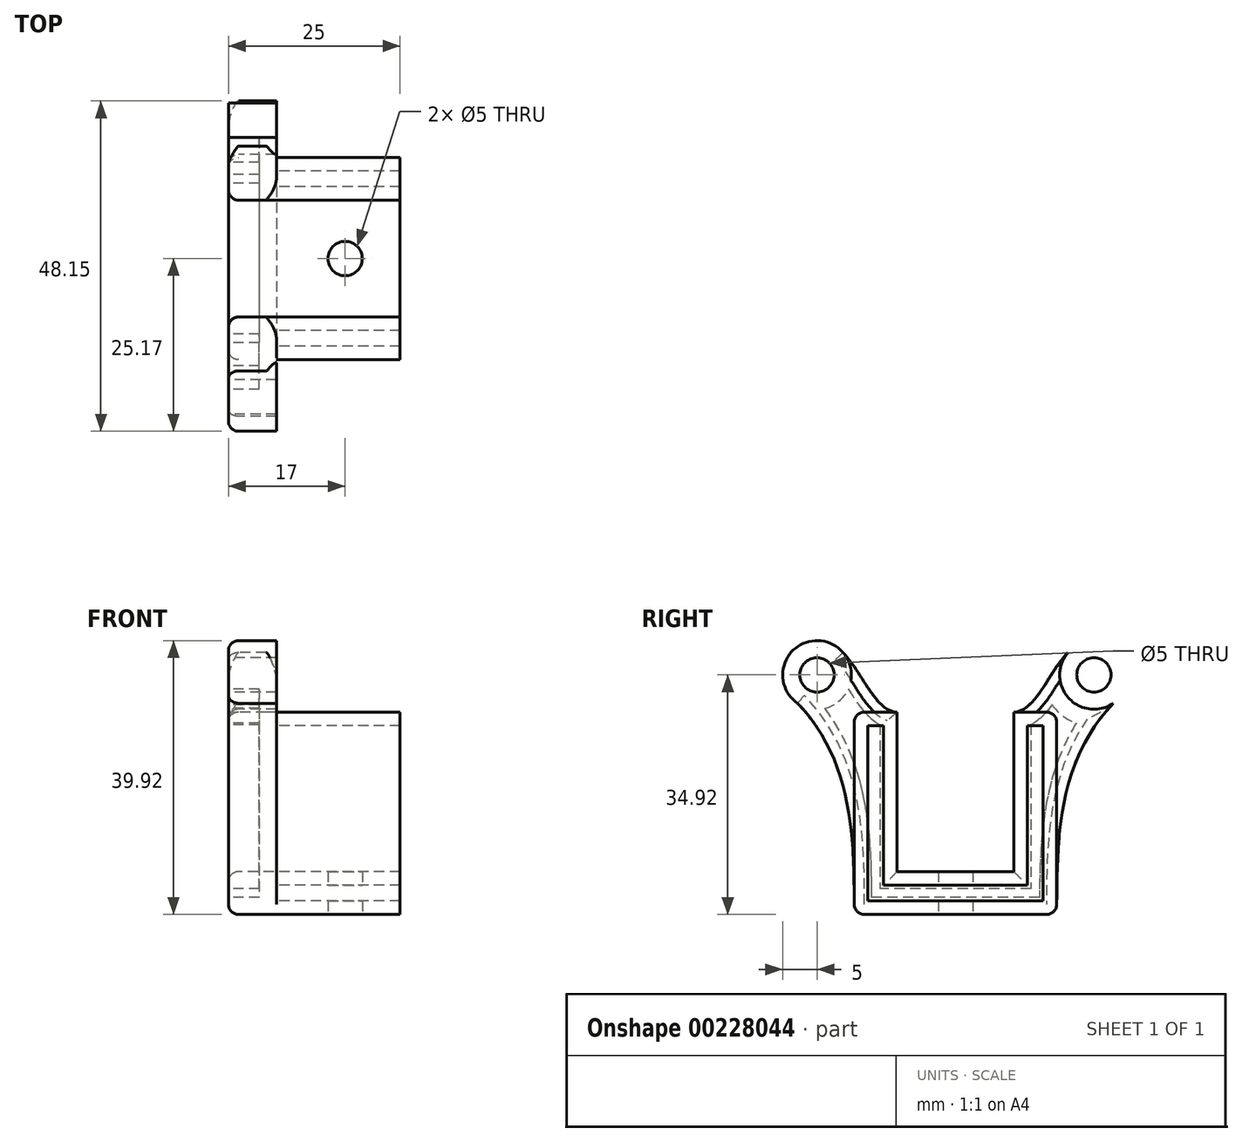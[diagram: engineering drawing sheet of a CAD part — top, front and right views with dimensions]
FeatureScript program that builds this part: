
annotation { "Feature Type Name" : "Feature", "Feature Type Description" : "" }
export const myFeature = defineFeature(function(context is Context, id is Id, definition is map)
    precondition{}
    {
        {
            var Q0;
            Q0=qCreatedBy(makeId("Right.planeOp"),FACE);
            var sketch = newSketch(context, id + "F0", { "sketchPlane" : qUnion([Q0])});
            skLineSegment(sketch, "E0.top", {"start": v(12.75, -12.75) * mm, "end": v(-12.75, -12.75) * mm});
            skLineSegment(sketch, "E0.left", {"start": v(12.75, 12.75) * mm, "end": v(12.75, -12.75) * mm});
            skLineSegment(sketch, "E0.right", {"start": v(-12.75, 12.75) * mm, "end": v(-12.75, -12.75) * mm});
            skPoint(sketch, "E0.middle", {"position": v(0, 0) * mm});
            skLineSegment(sketch, "E1.0", {"start": v(10.5, 12.75) * mm, "end": v(10.5, -10.5) * mm});
            skLineSegment(sketch, "E1.1", {"start": v(10.5, -10.5) * mm, "end": v(-10.5, -10.5) * mm});
            skLineSegment(sketch, "E1.2", {"start": v(-10.5, 12.75) * mm, "end": v(-10.5, -10.5) * mm});
            skLineSegment(sketch, "E2", {"start": v(-12.75, 12.75) * mm, "end": v(-10.5, 12.75) * mm});
            skLineSegment(sketch, "E3", {"start": v(10.5, 12.75) * mm, "end": v(12.75, 12.75) * mm});
            skLineSegment(sketch, "E4.0", {"start": v(-14.75, 14.75) * mm, "end": v(-8.5, 14.75) * mm});
            skLineSegment(sketch, "E4.1", {"start": v(-14.75, 14.75) * mm, "end": v(-14.75, -14.75) * mm});
            skLineSegment(sketch, "E4.2", {"start": v(-8.5, 14.75) * mm, "end": v(-8.5, -8.5) * mm});
            skLineSegment(sketch, "E4.3", {"start": v(14.75, -14.75) * mm, "end": v(-14.75, -14.75) * mm});
            skLineSegment(sketch, "E4.4", {"start": v(8.5, -8.5) * mm, "end": v(-8.5, -8.5) * mm});
            skLineSegment(sketch, "E4.5", {"start": v(8.5, 14.75) * mm, "end": v(8.5, -8.5) * mm});
            skLineSegment(sketch, "E4.6", {"start": v(8.5, 14.75) * mm, "end": v(14.75, 14.75) * mm});
            skLineSegment(sketch, "E4.7", {"start": v(14.75, 14.75) * mm, "end": v(14.75, -14.75) * mm});
            skLineSegment(sketch, "E5", {"start": v(-8.5, 14.75) * mm, "end": v(8.5, 14.75) * mm});
            skLineSegment(sketch, "E6", {"start": v(14.75, -14.75) * mm, "end": v(-49.35, 49.35) * mm, "construction": true});
            skLineSegment(sketch, "E7", {"start": v(-14.75, -14.75) * mm, "end": v(48.22, 48.22) * mm, "construction": true});
            skLineSegment(sketch, "E8", {"start": v(-40.93, 20.17) * mm, "end": v(49.97, 20.17) * mm, "construction": true});
            skCircle(sketch, "E9", {"center": v(-20.17, 20.17) * mm, "radius": 5 * mm});
            skLineSegment(sketch, "E10", {"start": v(0, 73.34) * mm, "end": v(0, -65.97) * mm, "construction": true});
            skPoint(sketch, "E11.0.internal.snap0", {"position": v(-17.3, 17.3) * mm});
            skFitSpline(sketch, "E11", {"points": [v(-24.26, 17.3) * mm, v(-14.75, -14.75) * mm], "startDerivative": vector(28.54, -26.5) * mm, "endDerivative": vector(0, -33.68) * mm});
            skFitSpline(sketch, "E12", {"points": [v(-16.39, 23.44) * mm, v(-8.5, 14.75) * mm], "startDerivative": vector(8.29, -8.38) * mm, "endDerivative": vector(9.37, 0) * mm});
            skCircle(sketch, "E13", {"center": v(-20.17, 20.17) * mm, "radius": 2.5 * mm});
            skFitSpline(sketch, "E14.MirrorCS", {"points": [v(16.39, 23.44) * mm, v(8.5, 14.75) * mm], "startDerivative": vector(-8.29, -8.38) * mm, "endDerivative": vector(-9.37, 0) * mm});
            skFitSpline(sketch, "E15.MirrorCS", {"points": [v(24.26, 17.3) * mm, v(14.75, -14.75) * mm], "startDerivative": vector(-28.54, -26.5) * mm, "endDerivative": vector(0, -33.68) * mm});
            skCircle(sketch, "E16.MirrorC", {"center": v(20.17, 20.17) * mm, "radius": 2.5 * mm});
            skCircle(sketch, "E17.MirrorC", {"center": v(20.17, 20.17) * mm, "radius": 5 * mm});
            skSolve(sketch);
        }
        {
            var Q0;
            Q0=makeQuery(id+"F0.imprint","IMPRINT",FACE,{"disambiguationData":[TD([[makeQuery(id+"F0.imprint","IMPRINT",EDGE,{"derivedFrom":sQuery(id+"F0.wireOp",EDGE,"E0.top")}),1.0]])]});
            extrude(context, id + "F1", {"entities" : qUnion([Q0]), "depth" : 25 * mm});
        }
        {
            var Q0;
            Q0=makeQuery(id+"F0.imprint","IMPRINT",FACE,{"disambiguationData":[TD([[makeQuery(id+"F0.imprint","IMPRINT",EDGE,{"derivedFrom":sQuery(id+"F0.wireOp",EDGE,"E4.0")}),1.0]])]});
            var Q1;
            Q1=makeQuery(id+"F0.imprint","IMPRINT",FACE,{"disambiguationData":[TD([[makeQuery(id+"F0.imprint","IMPRINT",EDGE,{"derivedFrom":sQuery(id+"F0.wireOp",EDGE,"E13")}),-1.0]])]});
            var Q2;
            {var subQ5=sQuery(id+"F0.wireOp",EDGE,"E4.7");Q2=makeQuery(id+"F0.imprint","IMPRINT",FACE,{"disambiguationData":[TD([[makeQuery(id+"F0.imprint","IMPRINT",EDGE,{"derivedFrom":subQ5}),1.0]])]});}
            var Q3;
            Q3=makeQuery(id+"F0.imprint","IMPRINT",FACE,{"disambiguationData":[TD([[makeQuery(id+"F0.imprint","IMPRINT",EDGE,{"derivedFrom":sQuery(id+"F0.wireOp",EDGE,"E16.MirrorC")}),1.0]])]});
            var Q4;
            Q4=makeQuery(id+"F0.imprint","IMPRINT",FACE,{"disambiguationData":[TD([[makeQuery(id+"F0.imprint","IMPRINT",EDGE,{"derivedFrom":sQuery(id+"F0.wireOp",EDGE,"E0.top")}),-1.0]])]});
            extrude(context, id + "F2", {"entities" : qUnion([Q0, Q1, Q2, Q3, Q4]), "operationType" : NewBodyOperationType.ADD, "depth" : 7 * mm});
        }
        {
            var Q0;
            {var subQ0=sQuery(id+"F0.wireOp",EDGE,"E14.MirrorCS");var subQ1=sQuery(id+"F0.wireOp",EDGE,"E4.7");var subQ2=sQuery(id+"F0.wireOp",EDGE,"E4.6");var subQ3=sQuery(id+"F0.wireOp",EDGE,"E4.1");var subQ4=sQuery(id+"F0.wireOp",EDGE,"E4.0");var subQ5=sQuery(id+"F0.wireOp",EDGE,"E3");var subQ6=sQuery(id+"F0.wireOp",EDGE,"E2");var subQ7=sQuery(id+"F0.wireOp",EDGE,"E1.2");var subQ8=sQuery(id+"F0.wireOp",EDGE,"E1.1");var subQ9=sQuery(id+"F0.wireOp",EDGE,"E1.0");var subQ10=sQuery(id+"F0.wireOp",EDGE,"E0.right");var subQ11=sQuery(id+"F0.wireOp",EDGE,"E0.left");var subQ12=sQuery(id+"F0.wireOp",EDGE,"E0.top");Q0=makeQuery(id+"F2.boolean.opBoolean","MERGE",FACE,{"derivedFrom":[makeQuery(id+"F1.opExtrude","CAP_FACE",FACE,{"disambiguationData":[OSD([subQ12,subQ11,subQ10,subQ9,subQ8,subQ7,subQ6,subQ5,subQ4,subQ3,sQuery(id+"F0.wireOp",EDGE,"E4.2"),sQuery(id+"F0.wireOp",EDGE,"E4.3"),sQuery(id+"F0.wireOp",EDGE,"E4.4"),sQuery(id+"F0.wireOp",EDGE,"E4.5"),subQ2,subQ1,subQ0])],"isStart":true}),makeQuery(id+"F2.opExtrude","CAP_FACE",FACE,{"disambiguationData":[OSD([subQ12,subQ11,subQ10,subQ9,subQ8,subQ7,subQ6,subQ5])],"isStart":true}),makeQuery(id+"F2.opExtrude","CAP_FACE",FACE,{"disambiguationData":[OSD([subQ4,subQ3,sQuery(id+"F0.wireOp",EDGE,"E9"),sQuery(id+"F0.wireOp",EDGE,"E11"),sQuery(id+"F0.wireOp",EDGE,"E12"),sQuery(id+"F0.wireOp",EDGE,"E13")])],"isStart":true}),makeQuery(id+"F2.opExtrude","CAP_FACE",FACE,{"disambiguationData":[OSD([subQ2,subQ1,subQ0,sQuery(id+"F0.wireOp",EDGE,"E15.MirrorCS"),sQuery(id+"F0.wireOp",EDGE,"E16.MirrorC"),sQuery(id+"F0.wireOp",EDGE,"E17.MirrorC")])],"isStart":true})]});}
            shell(context, id + "F3", {"entities" : qUnion([Q0]), "thickness" : 2.5 * mm});
        }
        {
            var Q0;
            Q0=makeQuery(id+"F1.opExtrude","SWEPT_FACE",FACE,{"disambiguationData":[OSD([sQuery(id+"F0.wireOp",EDGE,"E4.3")])]});
            var sketch = newSketch(context, id + "F4", { "sketchPlane" : qUnion([Q0])});
            skCircle(sketch, "E18", {"center": v(17, 0) * mm, "radius": 1.5 * mm});
            skSolve(sketch);
        }
        {
            var Q0;
            Q0=sQuery(id+"F4.wireOp",VERTEX,"E18.center");
            var Q1;
            Q1=makeQuery(id+"F1.opExtrude","SWEPT_BODY",BODY,{"disambiguationData":[OSD([sQuery(id+"F0.wireOp",EDGE,"E0.top"),sQuery(id+"F0.wireOp",EDGE,"E0.left"),sQuery(id+"F0.wireOp",EDGE,"E0.right"),sQuery(id+"F0.wireOp",EDGE,"E1.0"),sQuery(id+"F0.wireOp",EDGE,"E1.1"),sQuery(id+"F0.wireOp",EDGE,"E1.2"),sQuery(id+"F0.wireOp",EDGE,"E2"),sQuery(id+"F0.wireOp",EDGE,"E3"),sQuery(id+"F0.wireOp",EDGE,"E4.0"),sQuery(id+"F0.wireOp",EDGE,"E4.1"),sQuery(id+"F0.wireOp",EDGE,"E4.2"),sQuery(id+"F0.wireOp",EDGE,"E4.3"),sQuery(id+"F0.wireOp",EDGE,"E4.4"),sQuery(id+"F0.wireOp",EDGE,"E4.5"),sQuery(id+"F0.wireOp",EDGE,"E4.6"),sQuery(id+"F0.wireOp",EDGE,"E4.7"),sQuery(id+"F0.wireOp",EDGE,"E14.MirrorCS")])]});
            hole(context, id + "F5", {"style" : HoleStyle.SIMPLE, "endStyle" : HoleEndStyle.THROUGH, "holeDiameter" : 5 * mm, "locations" : qUnion([Q0]), "scope" : qUnion([Q1]), "isTappedThrough" : true});
        }
        {
            var Q0;
            Q0=makeQuery(id+"F2.opExtrude","CAP_EDGE",EDGE,{"disambiguationData":[OSD([sQuery(id+"F0.wireOp",EDGE,"E15.MirrorCS")])],"isStart":true});
            var Q1;
            Q1=makeQuery(id+"F1.opExtrude","CAP_EDGE",EDGE,{"disambiguationData":[OSD([sQuery(id+"F0.wireOp",EDGE,"E4.3")])],"isStart":true});
            var Q2;
            Q2=makeQuery(id+"F2.opExtrude","CAP_EDGE",EDGE,{"disambiguationData":[OSD([sQuery(id+"F0.wireOp",EDGE,"E11")])],"isStart":true});
            var Q3;
            Q3=makeQuery(id+"F2.opExtrude","CAP_EDGE",EDGE,{"disambiguationData":[OSD([sQuery(id+"F0.wireOp",EDGE,"E9")])],"isStart":true});
            var Q4;
            {var subQ0=sQuery(id+"F0.wireOp",EDGE,"E14.MirrorCS");Q4=makeQuery(id+"F2.boolean.opBoolean","MERGE",EDGE,{"derivedFrom":[makeQuery(id+"F1.opExtrude","CAP_EDGE",EDGE,{"disambiguationData":[OSD([subQ0])],"isStart":true}),makeQuery(id+"F2.opExtrude","CAP_EDGE",EDGE,{"disambiguationData":[OSD([subQ0])],"isStart":true})]});}
            var Q5;
            Q5=makeQuery(id+"F2.opExtrude","CAP_EDGE",EDGE,{"disambiguationData":[OSD([sQuery(id+"F0.wireOp",EDGE,"E17.MirrorC")])],"isStart":true});
            var Q6;
            Q6=makeQuery(id+"F1.opExtrude","CAP_EDGE",EDGE,{"disambiguationData":[OSD([sQuery(id+"F0.wireOp",EDGE,"E4.2")])],"isStart":true});
            var Q7;
            Q7=makeQuery(id+"F1.opExtrude","CAP_EDGE",EDGE,{"disambiguationData":[OSD([sQuery(id+"F0.wireOp",EDGE,"E4.5")])],"isStart":true});
            var Q8;
            Q8=makeQuery(id+"F1.opExtrude","CAP_EDGE",EDGE,{"disambiguationData":[OSD([sQuery(id+"F0.wireOp",EDGE,"E4.4")])],"isStart":true});
            var Q9;
            Q9=makeQuery(id+"F2.opExtrude","CAP_EDGE",EDGE,{"disambiguationData":[OSD([sQuery(id+"F0.wireOp",EDGE,"E12")])],"isStart":true});
            var Q10;
            {var subQ0=sQuery(id+"F0.wireOp",EDGE,"E15.MirrorCS");var subQ1=sQuery(id+"F0.wireOp",EDGE,"E4.7");var subQ2=sQuery(id+"F0.wireOp",EDGE,"E4.3");Q10=makeQuery(id+"F2.boolean.opBoolean","MERGE",EDGE,{"derivedFrom":[makeQuery(id+"F1.opExtrude","SWEPT_EDGE",EDGE,{"disambiguationData":[OSD([subQ2,subQ1,subQ0])]}),makeQuery(id+"F2.opExtrude","SWEPT_EDGE",EDGE,{"disambiguationData":[OSD([subQ2,subQ1,subQ0])]})]});}
            var Q11;
            {var subQ0=sQuery(id+"F0.wireOp",EDGE,"E11");var subQ1=sQuery(id+"F0.wireOp",EDGE,"E4.3");var subQ2=sQuery(id+"F0.wireOp",EDGE,"E4.1");Q11=makeQuery(id+"F2.boolean.opBoolean","MERGE",EDGE,{"derivedFrom":[makeQuery(id+"F1.opExtrude","SWEPT_EDGE",EDGE,{"disambiguationData":[OSD([subQ2,subQ1,subQ0])]}),makeQuery(id+"F2.opExtrude","SWEPT_EDGE",EDGE,{"disambiguationData":[OSD([subQ2,subQ1,subQ0])]})]});}
            var Q12;
            Q12=makeQuery(id+"F2.opExtrude","CAP_EDGE",EDGE,{"disambiguationData":[OSD([sQuery(id+"F0.wireOp",EDGE,"E12")])],"isStart":false});
            var Q13;
            Q13=makeQuery(id+"F2.opExtrude","CAP_EDGE",EDGE,{"disambiguationData":[OSD([sQuery(id+"F0.wireOp",EDGE,"E14.MirrorCS")])],"isStart":false});
            var Q14;
            Q14=makeQuery(id+"F1.opExtrude","SWEPT_EDGE",EDGE,{"disambiguationData":[OSD([sQuery(id+"F0.wireOp",EDGE,"E4.0"),sQuery(id+"F0.wireOp",EDGE,"E4.1")])]});
            var Q15;
            Q15=makeQuery(id+"F1.opExtrude","SWEPT_EDGE",EDGE,{"disambiguationData":[OSD([sQuery(id+"F0.wireOp",EDGE,"E4.6"),sQuery(id+"F0.wireOp",EDGE,"E4.7")])]});
            fillet(context, id + "F6", {"entities" : qUnion([Q0, Q1, Q2, Q3, Q4, Q5, Q6, Q7, Q8, Q9, Q10, Q11, Q12, Q13, Q14, Q15]), "radius" : 1.5 * mm, "tangentPropagation" : true, "allowEdgeOverflow" : false});
        }
    });
